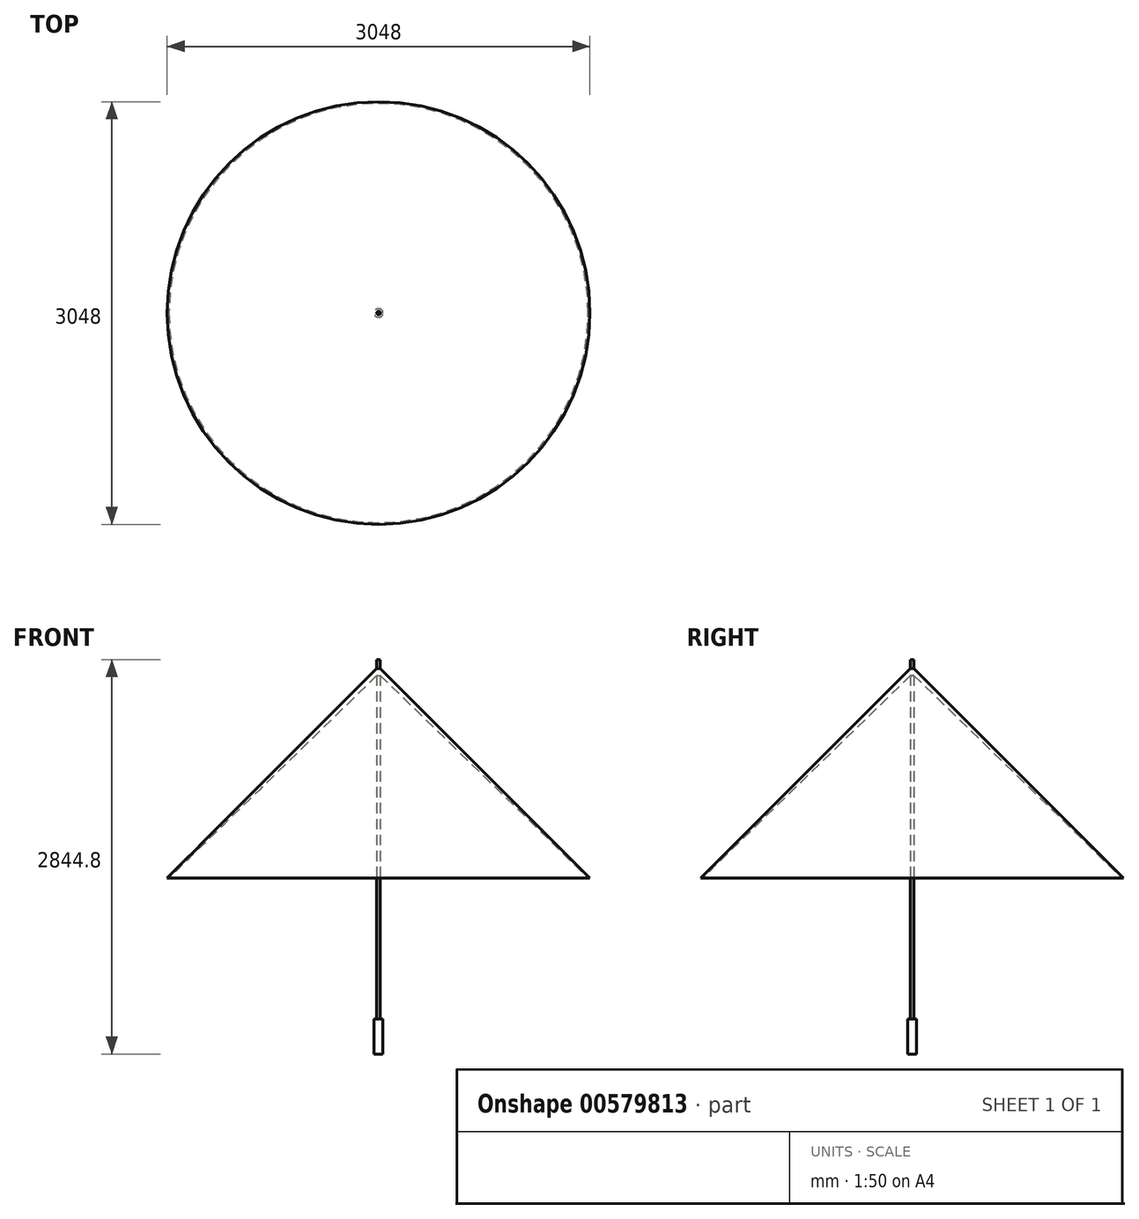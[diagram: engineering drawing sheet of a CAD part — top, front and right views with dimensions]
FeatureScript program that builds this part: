
annotation { "Feature Type Name" : "Feature", "Feature Type Description" : "" }
export const myFeature = defineFeature(function(context is Context, id is Id, definition is map)
    precondition{}
    {
        {
            var Q0;
            Q0=qCreatedBy(makeId("Front.planeOp"),FACE);
            var sketch = newSketch(context, id + "F0", { "sketchPlane" : qUnion([Q0])});
            skLineSegment(sketch, "E0", {"start": v(0, 0) * mm, "end": v(1524, 0) * mm});
            skLineSegment(sketch, "E1", {"start": v(0, 0) * mm, "end": v(0, 1524) * mm});
            skLineSegment(sketch, "E2", {"start": v(0, 1524) * mm, "end": v(1524, 0) * mm});
            skSolve(sketch);
        }
        {
            var Q0;
            Q0=makeQuery(id+"F0.imprint","IMPRINT",FACE,{"disambiguationData":[TD([[makeQuery(id+"F0.imprint","IMPRINT",EDGE,{"derivedFrom":sQuery(id+"F0.wireOp",EDGE,"E0")}),1.0]])]});
            var Q1;
            Q1=sQuery(id+"F0.wireOp",EDGE,"E1");
            revolve(context, id + "F1", {"entities" : qUnion([Q0]), "axis" : qUnion([Q1]), "revolveType" : RevolveType.FULL});
        }
        {
            var Q0;
            Q0=qCreatedBy(makeId("Front.planeOp"),FACE);
            var sketch = newSketch(context, id + "F2", { "sketchPlane" : qUnion([Q0])});
            skLineSegment(sketch, "E3", {"start": v(0, 0) * mm, "end": v(1511.3, 0) * mm});
            skLineSegment(sketch, "E4", {"start": v(1511.3, 0) * mm, "end": v(0, 1472.76) * mm});
            skLineSegment(sketch, "E5", {"start": v(0, 1472.76) * mm, "end": v(0, 0) * mm});
            skSolve(sketch);
        }
        {
            var Q0;
            Q0 = qSketchRegion(id + "F2", true);
            var Q1;
            Q1=sQuery(id+"F2.wireOp",EDGE,"E5");
            revolve(context, id + "F3", {"operationType" : NewBodyOperationType.REMOVE, "entities" : qUnion([Q0]), "axis" : qUnion([Q1]), "revolveType" : RevolveType.FULL});
        }
        {
            var Q0;
            Q0=makeQuery(id+"F1.opRevolve","SWEPT_FACE",FACE,{"disambiguationData":[OSD([sQuery(id+"F0.wireOp",EDGE,"E0")])]});
            var sketch = newSketch(context, id + "F4", { "sketchPlane" : qUnion([Q0])});
            skCircle(sketch, "E6", {"center": v(0, 0) * mm, "radius": 12.7 * mm});
            skCircle(sketch, "E7", {"center": v(0, 0) * mm, "radius": 19.05 * mm});
            skSolve(sketch);
        }
        {
            var Q0;
            Q0=makeQuery(id+"F4.imprint","IMPRINT",FACE,{"disambiguationData":[TD([[makeQuery(id+"F4.imprint","IMPRINT",EDGE,{"derivedFrom":sQuery(id+"F4.wireOp",EDGE,"E6")}),1.0]])]});
            extrude(context, id + "F5", {"entities" : qUnion([Q0]), "operationType" : NewBodyOperationType.ADD, "oppositeDirection" : true, "depth" : 1574.8 * mm, "offsetDistance" : 25.4 * mm, "hasSecondDirection" : true, "secondDirectionOppositeDirection" : false, "secondDirectionDepth" : 1016 * mm});
        }
        {
            var Q0;
            Q0=makeQuery(id+"F5.opExtrude","CAP_FACE",FACE,{"disambiguationData":[OSD([sQuery(id+"F4.wireOp",EDGE,"E6")])],"isStart":true});
            var sketch = newSketch(context, id + "F6", { "sketchPlane" : qUnion([Q0])});
            skCircle(sketch, "E8", {"center": v(0, 0) * mm, "radius": 31.75 * mm});
            skSolve(sketch);
        }
        {
            var Q0;
            Q0 = qSketchRegion(id + "F6", true);
            extrude(context, id + "F7", {"entities" : qUnion([Q0]), "operationType" : NewBodyOperationType.ADD, "depth" : 254 * mm, "offsetDistance" : 25.4 * mm});
        }
    });
